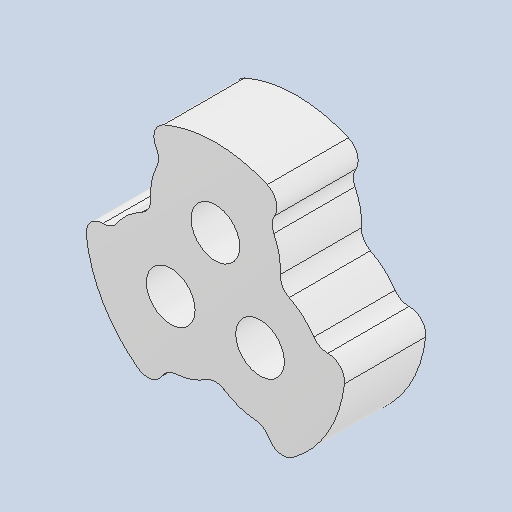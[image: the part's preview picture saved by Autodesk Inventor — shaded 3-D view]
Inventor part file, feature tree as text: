
AUTODESK INVENTOR PART (.ipt)
format: ipt  version: 2023 (Build 270158030, 158C)  size: 209,920 bytes
history: native  units: mm
features: sketch x4, extrude x3, projected_geometry x3, fillet x2, other x1
ambient origin geometry x8: Origin, YZ Plane, XZ Plane, XY Plane, X Axis, Y Axis, Z Axis, Center Point
bodies: Body1 (feature_tree)
feature tree (13):
  other  "ソリッド1"
  extrude  "押し出し1"  Depth=3.0mm
  sketch  "スケッチ2"
  extrude  "押し出し2"  Depth=3.0mm
  extrude  "押し出し3"  Depth=3.0mm
  fillet  "フィレット1"  Radius=2.5mm
  fillet  "フィレット2"  Radius=2.5mm
  sketch  "スケッチ1"
  projected_geometry  "投影ループ1"
  sketch  "スケッチ3"
  projected_geometry  "投影ループ2"
  sketch  "スケッチ4"
  projected_geometry  "投影ループ3"
